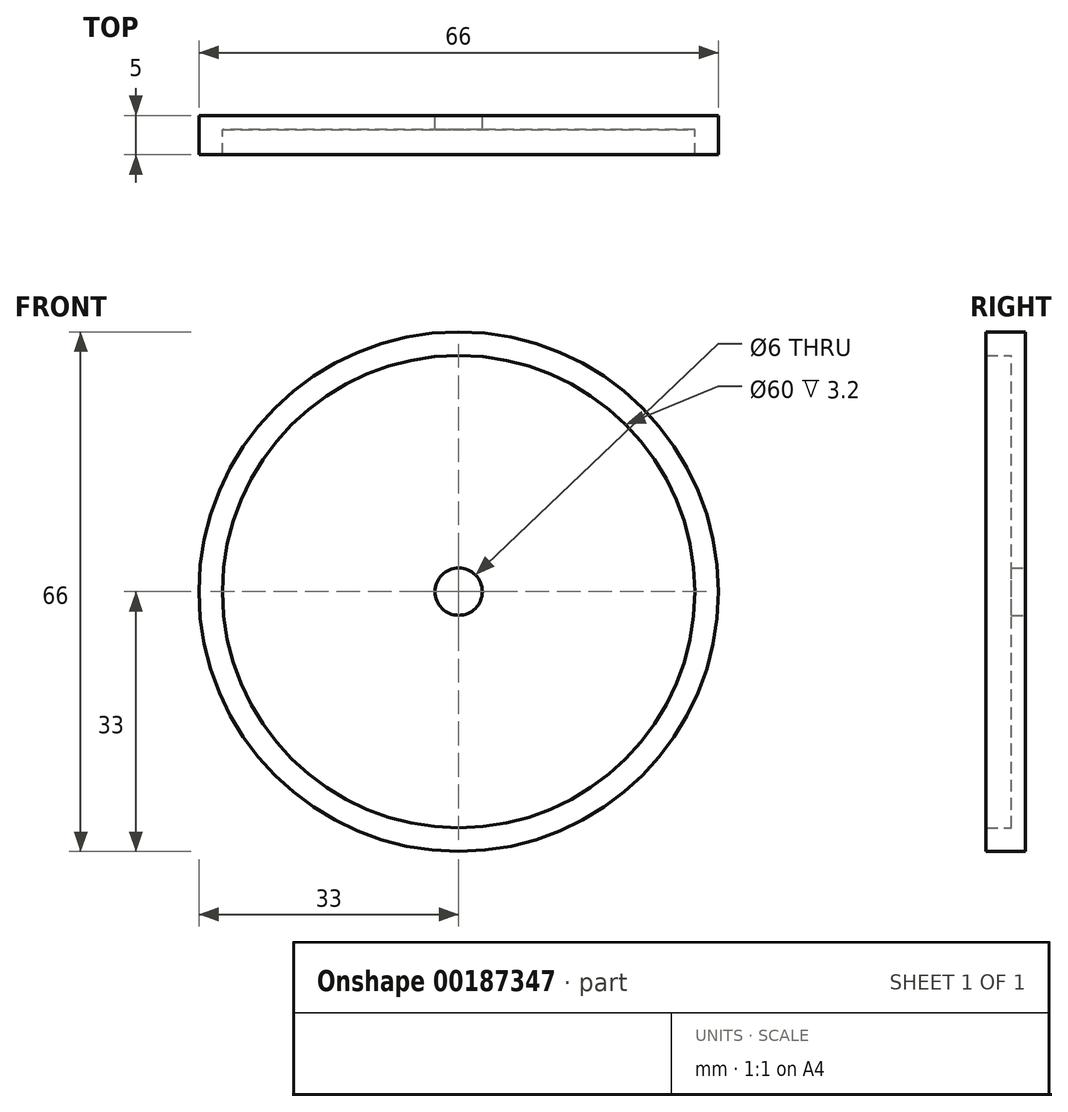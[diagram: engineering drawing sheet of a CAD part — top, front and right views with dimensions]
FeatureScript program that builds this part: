
annotation { "Feature Type Name" : "Feature", "Feature Type Description" : "" }
export const myFeature = defineFeature(function(context is Context, id is Id, definition is map)
    precondition{}
    {
        {
            var Q0;
            Q0=qCreatedBy(makeId("Front.planeOp"),FACE);
            var sketch = newSketch(context, id + "F0", { "sketchPlane" : qUnion([Q0])});
            skCircle(sketch, "E0", {"center": v(0, 0) * mm, "radius": 33 * mm});
            skCircle(sketch, "E1", {"center": v(0, 0) * mm, "radius": 30 * mm});
            skCircle(sketch, "E2", {"center": v(0, 0) * mm, "radius": 3 * mm});
            skSolve(sketch);
        }
        {
            var Q0;
            Q0=makeQuery(id+"F0.imprint","IMPRINT",FACE,{"disambiguationData":[TD([[makeQuery(id+"F0.imprint","IMPRINT",EDGE,{"derivedFrom":sQuery(id+"F0.wireOp",EDGE,"E0")}),1.0]])]});
            var Q1;
            Q1=makeQuery(id+"F0.imprint","IMPRINT",FACE,{"disambiguationData":[TD([[makeQuery(id+"F0.imprint","IMPRINT",EDGE,{"derivedFrom":sQuery(id+"F0.wireOp",EDGE,"E1")}),1.0]])]});
            extrude(context, id + "F1", {"entities" : qUnion([Q0, Q1]), "depth" : 1.8 * mm});
        }
        {
            var Q0;
            Q0 = qSketchRegion(id + "F0", true);
            extrude(context, id + "F2", {"entities" : qUnion([Q0]), "operationType" : NewBodyOperationType.ADD, "depth" : 5 * mm});
        }
    });
